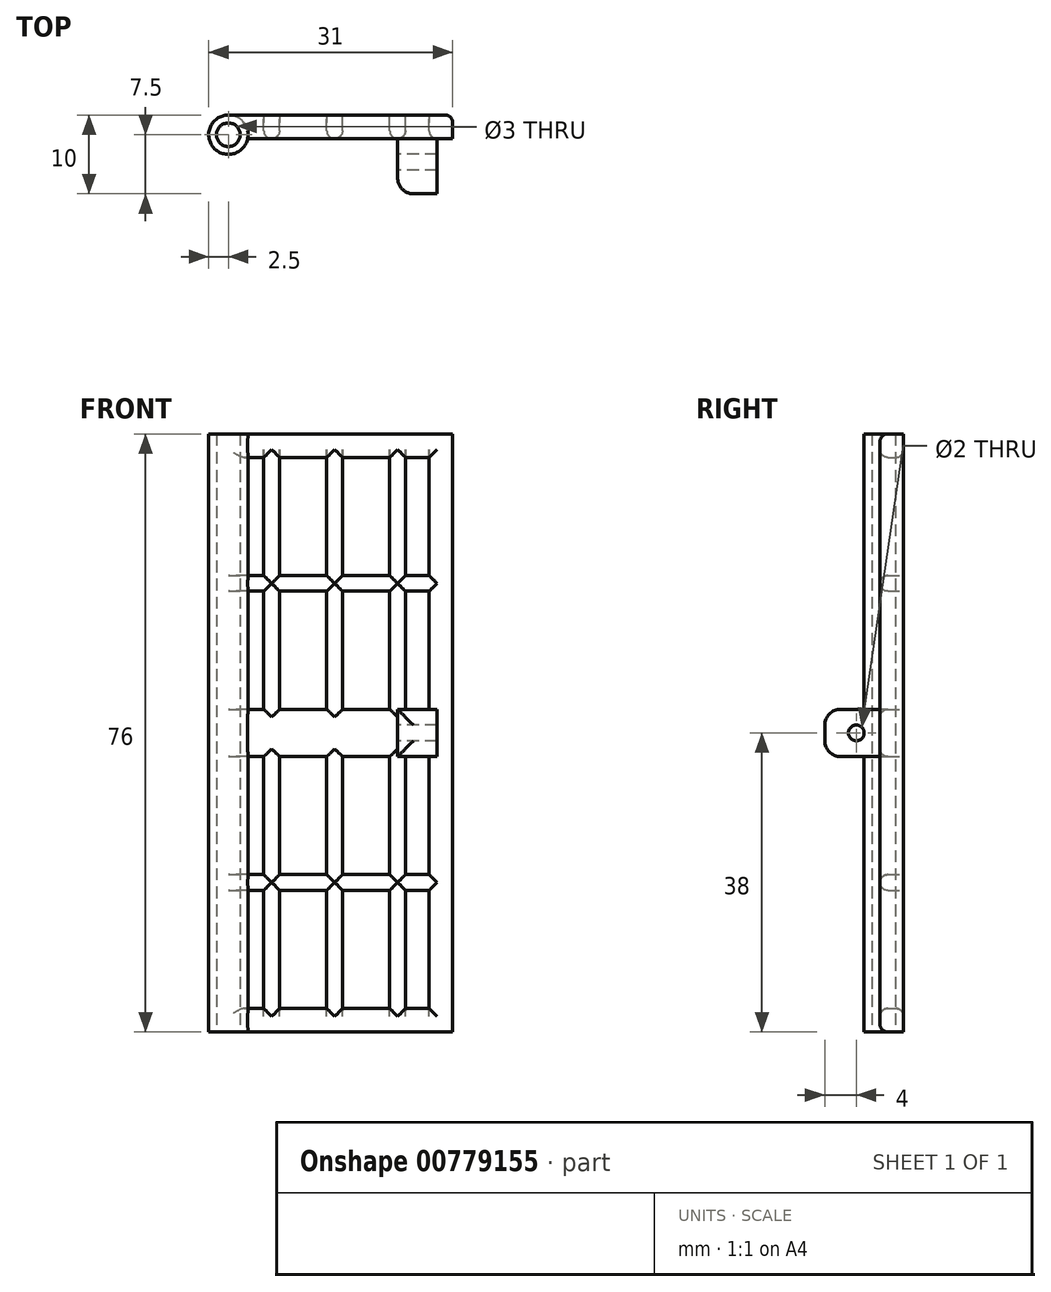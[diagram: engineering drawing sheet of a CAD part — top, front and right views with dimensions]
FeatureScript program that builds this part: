
annotation { "Feature Type Name" : "Feature", "Feature Type Description" : "" }
export const myFeature = defineFeature(function(context is Context, id is Id, definition is map)
    precondition{}
    {
        {
            var Q0;
            Q0=qCreatedBy(makeId("Front.planeOp"),FACE);
            var sketch = newSketch(context, id + "F0", { "sketchPlane" : qUnion([Q0])});
            skLineSegment(sketch, "E0.bottom", {"start": v(0, 0) * mm, "end": v(31, 0) * mm});
            skLineSegment(sketch, "E0.top", {"start": v(0, 76) * mm, "end": v(31, 76) * mm});
            skLineSegment(sketch, "E0.left", {"start": v(0, 0) * mm, "end": v(0, 76) * mm});
            skLineSegment(sketch, "E0.right", {"start": v(31, 0) * mm, "end": v(31, 76) * mm});
            skLineSegment(sketch, "E1.bottom", {"start": v(5, 73) * mm, "end": v(28, 73) * mm});
            skLineSegment(sketch, "E1.top", {"start": v(5, 3) * mm, "end": v(28, 3) * mm});
            skLineSegment(sketch, "E1.left", {"start": v(5, 73) * mm, "end": v(5, 3) * mm});
            skLineSegment(sketch, "E1.right", {"start": v(28, 73) * mm, "end": v(28, 3) * mm});
            skArc(sketch, "E2", {"start": v(23, 76) * mm, "mid": v(31, 84) * mm, "end": v(39, 76) * mm});
            skArc(sketch, "E3", {"start": v(25, 76) * mm, "mid": v(31, 82) * mm, "end": v(37, 76) * mm});
            skArc(sketch, "E4", {"start": v(17, 76) * mm, "mid": v(31, 90) * mm, "end": v(45, 76) * mm});
            skArc(sketch, "E5", {"start": v(15, 76) * mm, "mid": v(31, 92) * mm, "end": v(47, 76) * mm});
            skArc(sketch, "E6", {"start": v(9, 76) * mm, "mid": v(31, 98) * mm, "end": v(53, 76) * mm});
            skArc(sketch, "E7", {"start": v(7, 76) * mm, "mid": v(31, 100) * mm, "end": v(55, 76) * mm});
            skLineSegment(sketch, "E8", {"start": v(7, 76) * mm, "end": v(7, 3) * mm});
            skLineSegment(sketch, "E9", {"start": v(9, 76) * mm, "end": v(9, 3) * mm});
            skLineSegment(sketch, "E10", {"start": v(15, 76) * mm, "end": v(15, 3) * mm});
            skLineSegment(sketch, "E11", {"start": v(17, 76) * mm, "end": v(17, 3) * mm});
            skLineSegment(sketch, "E12", {"start": v(23, 76) * mm, "end": v(23, 3) * mm});
            skLineSegment(sketch, "E13", {"start": v(25, 76) * mm, "end": v(25, 3) * mm});
            skLineSegment(sketch, "E14", {"start": v(5, 58) * mm, "end": v(28, 58) * mm});
            skLineSegment(sketch, "E15", {"start": v(5, 56) * mm, "end": v(28, 56) * mm});
            skLineSegment(sketch, "E16", {"start": v(5, 41) * mm, "end": v(28, 41) * mm});
            skLineSegment(sketch, "E17", {"start": v(5, 35) * mm, "end": v(28, 35) * mm});
            skLineSegment(sketch, "E18", {"start": v(5, 18) * mm, "end": v(28, 18) * mm});
            skLineSegment(sketch, "E19", {"start": v(5, 20) * mm, "end": v(28, 20) * mm});
            skSolve(sketch);
        }
        {
            var Q0;
            {var subQ0=sQuery(id+"F0.wireOp",EDGE,"E10");var subQ1=sQuery(id+"F0.wireOp",EDGE,"E0.top");var subQ2=makeQuery(id+"F0.imprint","INTERSECT",VERTEX,{"derivedFrom":[subQ1,subQ0]});Q0=makeQuery(id+"F0.imprint","IMPRINT",FACE,{"disambiguationData":[TD([[makeQuery(id+"F0.imprint","IMPRINT",EDGE,{"disambiguationData":[TD([[subQ2,1.0]])],"derivedFrom":subQ1}),-1.0]])]});}
            var Q1;
            {var subQ0=sQuery(id+"F0.wireOp",EDGE,"E14");var subQ1=sQuery(id+"F0.wireOp",EDGE,"E9");var subQ2=makeQuery(id+"F0.imprint","INTERSECT",VERTEX,{"derivedFrom":[subQ1,subQ0]});Q1=makeQuery(id+"F0.imprint","IMPRINT",FACE,{"disambiguationData":[TD([[makeQuery(id+"F0.imprint","IMPRINT",EDGE,{"disambiguationData":[TD([[subQ2,-1.0]])],"derivedFrom":subQ1}),1.0]])]});}
            var Q2;
            {var subQ0=sQuery(id+"F0.wireOp",EDGE,"E16");var subQ1=sQuery(id+"F0.wireOp",EDGE,"E9");var subQ2=makeQuery(id+"F0.imprint","INTERSECT",VERTEX,{"derivedFrom":[subQ1,subQ0]});Q2=makeQuery(id+"F0.imprint","IMPRINT",FACE,{"disambiguationData":[TD([[makeQuery(id+"F0.imprint","IMPRINT",EDGE,{"disambiguationData":[TD([[subQ2,-1.0]])],"derivedFrom":subQ1}),1.0]])]});}
            var Q3;
            {var subQ0=sQuery(id+"F0.wireOp",EDGE,"E19");var subQ1=sQuery(id+"F0.wireOp",EDGE,"E9");var subQ2=makeQuery(id+"F0.imprint","INTERSECT",VERTEX,{"derivedFrom":[subQ1,subQ0]});Q3=makeQuery(id+"F0.imprint","IMPRINT",FACE,{"disambiguationData":[TD([[makeQuery(id+"F0.imprint","IMPRINT",EDGE,{"disambiguationData":[TD([[subQ2,-1.0]])],"derivedFrom":subQ1}),1.0]])]});}
            var Q4;
            Q4=makeQuery(id+"F0.imprint","IMPRINT",FACE,{"disambiguationData":[TD([[makeQuery(id+"F0.imprint","IMPRINT",EDGE,{"derivedFrom":sQuery(id+"F0.wireOp",EDGE,"E0.bottom")}),1.0]])]});
            var Q5;
            {var subQ0=sQuery(id+"F0.wireOp",EDGE,"E9");var subQ1=sQuery(id+"F0.wireOp",EDGE,"E0.top");var subQ2=makeQuery(id+"F0.imprint","INTERSECT",VERTEX,{"derivedFrom":[subQ1,subQ0]});Q5=makeQuery(id+"F0.imprint","IMPRINT",FACE,{"disambiguationData":[TD([[makeQuery(id+"F0.imprint","IMPRINT",EDGE,{"disambiguationData":[TD([[subQ2,1.0]])],"derivedFrom":subQ1}),-1.0]])]});}
            var Q6;
            {var subQ0=sQuery(id+"F0.wireOp",EDGE,"E11");var subQ1=sQuery(id+"F0.wireOp",EDGE,"E0.top");var subQ2=makeQuery(id+"F0.imprint","INTERSECT",VERTEX,{"derivedFrom":[subQ1,subQ0]});Q6=makeQuery(id+"F0.imprint","IMPRINT",FACE,{"disambiguationData":[TD([[makeQuery(id+"F0.imprint","IMPRINT",EDGE,{"disambiguationData":[TD([[subQ2,1.0]])],"derivedFrom":subQ1}),-1.0]])]});}
            var Q7;
            {var subQ0=sQuery(id+"F0.wireOp",EDGE,"E12");var subQ1=sQuery(id+"F0.wireOp",EDGE,"E0.top");var subQ2=makeQuery(id+"F0.imprint","INTERSECT",VERTEX,{"derivedFrom":[subQ1,subQ0]});Q7=makeQuery(id+"F0.imprint","IMPRINT",FACE,{"disambiguationData":[TD([[makeQuery(id+"F0.imprint","IMPRINT",EDGE,{"disambiguationData":[TD([[subQ2,1.0]])],"derivedFrom":subQ1}),-1.0]])]});}
            var Q8;
            {var subQ0=sQuery(id+"F0.wireOp",EDGE,"E12");var subQ1=sQuery(id+"F0.wireOp",EDGE,"E0.top");var subQ2=makeQuery(id+"F0.imprint","INTERSECT",VERTEX,{"derivedFrom":[subQ1,subQ0]});Q8=makeQuery(id+"F0.imprint","IMPRINT",FACE,{"disambiguationData":[TD([[makeQuery(id+"F0.imprint","IMPRINT",EDGE,{"disambiguationData":[TD([[subQ2,-1.0]])],"derivedFrom":subQ1}),-1.0]])]});}
            var Q9;
            {var subQ0=sQuery(id+"F0.wireOp",EDGE,"E8");var subQ1=sQuery(id+"F0.wireOp",EDGE,"E1.bottom");var subQ2=makeQuery(id+"F0.imprint","INTERSECT",VERTEX,{"derivedFrom":[subQ1,subQ0]});Q9=makeQuery(id+"F0.imprint","IMPRINT",FACE,{"disambiguationData":[TD([[makeQuery(id+"F0.imprint","IMPRINT",EDGE,{"disambiguationData":[TD([[subQ2,-1.0]])],"derivedFrom":subQ1}),-1.0]])]});}
            var Q10;
            {var subQ0=sQuery(id+"F0.wireOp",EDGE,"E10");var subQ1=sQuery(id+"F0.wireOp",EDGE,"E1.bottom");var subQ2=makeQuery(id+"F0.imprint","INTERSECT",VERTEX,{"derivedFrom":[subQ1,subQ0]});Q10=makeQuery(id+"F0.imprint","IMPRINT",FACE,{"disambiguationData":[TD([[makeQuery(id+"F0.imprint","IMPRINT",EDGE,{"disambiguationData":[TD([[subQ2,-1.0]])],"derivedFrom":subQ1}),-1.0]])]});}
            var Q11;
            {var subQ0=sQuery(id+"F0.wireOp",EDGE,"E12");var subQ1=sQuery(id+"F0.wireOp",EDGE,"E1.bottom");var subQ2=makeQuery(id+"F0.imprint","INTERSECT",VERTEX,{"derivedFrom":[subQ1,subQ0]});Q11=makeQuery(id+"F0.imprint","IMPRINT",FACE,{"disambiguationData":[TD([[makeQuery(id+"F0.imprint","IMPRINT",EDGE,{"disambiguationData":[TD([[subQ2,-1.0]])],"derivedFrom":subQ1}),-1.0]])]});}
            var Q12;
            {var subQ0=sQuery(id+"F0.wireOp",EDGE,"E14");var subQ1=sQuery(id+"F0.wireOp",EDGE,"E1.left");var subQ2=makeQuery(id+"F0.imprint","INTERSECT",VERTEX,{"derivedFrom":[subQ1,subQ0]});Q12=makeQuery(id+"F0.imprint","IMPRINT",FACE,{"disambiguationData":[TD([[makeQuery(id+"F0.imprint","IMPRINT",EDGE,{"disambiguationData":[TD([[subQ2,-1.0]])],"derivedFrom":subQ1}),1.0]])]});}
            var Q13;
            {var subQ0=sQuery(id+"F0.wireOp",EDGE,"E14");var subQ1=sQuery(id+"F0.wireOp",EDGE,"E8");var subQ2=makeQuery(id+"F0.imprint","INTERSECT",VERTEX,{"derivedFrom":[subQ1,subQ0]});Q13=makeQuery(id+"F0.imprint","IMPRINT",FACE,{"disambiguationData":[TD([[makeQuery(id+"F0.imprint","IMPRINT",EDGE,{"disambiguationData":[TD([[subQ2,-1.0]])],"derivedFrom":subQ1}),1.0]])]});}
            var Q14;
            {var subQ0=sQuery(id+"F0.wireOp",EDGE,"E14");var subQ1=sQuery(id+"F0.wireOp",EDGE,"E10");var subQ2=makeQuery(id+"F0.imprint","INTERSECT",VERTEX,{"derivedFrom":[subQ1,subQ0]});Q14=makeQuery(id+"F0.imprint","IMPRINT",FACE,{"disambiguationData":[TD([[makeQuery(id+"F0.imprint","IMPRINT",EDGE,{"disambiguationData":[TD([[subQ2,-1.0]])],"derivedFrom":subQ1}),1.0]])]});}
            var Q15;
            {var subQ0=sQuery(id+"F0.wireOp",EDGE,"E14");var subQ1=sQuery(id+"F0.wireOp",EDGE,"E11");var subQ2=makeQuery(id+"F0.imprint","INTERSECT",VERTEX,{"derivedFrom":[subQ1,subQ0]});Q15=makeQuery(id+"F0.imprint","IMPRINT",FACE,{"disambiguationData":[TD([[makeQuery(id+"F0.imprint","IMPRINT",EDGE,{"disambiguationData":[TD([[subQ2,-1.0]])],"derivedFrom":subQ1}),1.0]])]});}
            var Q16;
            {var subQ0=sQuery(id+"F0.wireOp",EDGE,"E14");var subQ1=sQuery(id+"F0.wireOp",EDGE,"E12");var subQ2=makeQuery(id+"F0.imprint","INTERSECT",VERTEX,{"derivedFrom":[subQ1,subQ0]});Q16=makeQuery(id+"F0.imprint","IMPRINT",FACE,{"disambiguationData":[TD([[makeQuery(id+"F0.imprint","IMPRINT",EDGE,{"disambiguationData":[TD([[subQ2,-1.0]])],"derivedFrom":subQ1}),1.0]])]});}
            var Q17;
            {var subQ0=sQuery(id+"F0.wireOp",EDGE,"E14");var subQ1=sQuery(id+"F0.wireOp",EDGE,"E1.right");var subQ2=makeQuery(id+"F0.imprint","INTERSECT",VERTEX,{"derivedFrom":[subQ1,subQ0]});Q17=makeQuery(id+"F0.imprint","IMPRINT",FACE,{"disambiguationData":[TD([[makeQuery(id+"F0.imprint","IMPRINT",EDGE,{"disambiguationData":[TD([[subQ2,-1.0]])],"derivedFrom":subQ1}),-1.0]])]});}
            var Q18;
            {var subQ0=sQuery(id+"F0.wireOp",EDGE,"E15");var subQ1=sQuery(id+"F0.wireOp",EDGE,"E10");var subQ2=makeQuery(id+"F0.imprint","INTERSECT",VERTEX,{"derivedFrom":[subQ1,subQ0]});Q18=makeQuery(id+"F0.imprint","IMPRINT",FACE,{"disambiguationData":[TD([[makeQuery(id+"F0.imprint","IMPRINT",EDGE,{"disambiguationData":[TD([[subQ2,-1.0]])],"derivedFrom":subQ1}),1.0]])]});}
            var Q19;
            {var subQ0=sQuery(id+"F0.wireOp",EDGE,"E15");var subQ1=sQuery(id+"F0.wireOp",EDGE,"E12");var subQ2=makeQuery(id+"F0.imprint","INTERSECT",VERTEX,{"derivedFrom":[subQ1,subQ0]});Q19=makeQuery(id+"F0.imprint","IMPRINT",FACE,{"disambiguationData":[TD([[makeQuery(id+"F0.imprint","IMPRINT",EDGE,{"disambiguationData":[TD([[subQ2,-1.0]])],"derivedFrom":subQ1}),1.0]])]});}
            var Q20;
            {var subQ0=sQuery(id+"F0.wireOp",EDGE,"E15");var subQ1=sQuery(id+"F0.wireOp",EDGE,"E8");var subQ2=makeQuery(id+"F0.imprint","INTERSECT",VERTEX,{"derivedFrom":[subQ1,subQ0]});Q20=makeQuery(id+"F0.imprint","IMPRINT",FACE,{"disambiguationData":[TD([[makeQuery(id+"F0.imprint","IMPRINT",EDGE,{"disambiguationData":[TD([[subQ2,-1.0]])],"derivedFrom":subQ1}),1.0]])]});}
            var Q21;
            {var subQ0=sQuery(id+"F0.wireOp",EDGE,"E16");var subQ1=sQuery(id+"F0.wireOp",EDGE,"E1.left");var subQ2=makeQuery(id+"F0.imprint","INTERSECT",VERTEX,{"derivedFrom":[subQ1,subQ0]});Q21=makeQuery(id+"F0.imprint","IMPRINT",FACE,{"disambiguationData":[TD([[makeQuery(id+"F0.imprint","IMPRINT",EDGE,{"disambiguationData":[TD([[subQ2,-1.0]])],"derivedFrom":subQ1}),1.0]])]});}
            var Q22;
            {var subQ0=sQuery(id+"F0.wireOp",EDGE,"E16");var subQ1=sQuery(id+"F0.wireOp",EDGE,"E8");var subQ2=makeQuery(id+"F0.imprint","INTERSECT",VERTEX,{"derivedFrom":[subQ1,subQ0]});Q22=makeQuery(id+"F0.imprint","IMPRINT",FACE,{"disambiguationData":[TD([[makeQuery(id+"F0.imprint","IMPRINT",EDGE,{"disambiguationData":[TD([[subQ2,-1.0]])],"derivedFrom":subQ1}),1.0]])]});}
            var Q23;
            {var subQ0=sQuery(id+"F0.wireOp",EDGE,"E16");var subQ1=sQuery(id+"F0.wireOp",EDGE,"E10");var subQ2=makeQuery(id+"F0.imprint","INTERSECT",VERTEX,{"derivedFrom":[subQ1,subQ0]});Q23=makeQuery(id+"F0.imprint","IMPRINT",FACE,{"disambiguationData":[TD([[makeQuery(id+"F0.imprint","IMPRINT",EDGE,{"disambiguationData":[TD([[subQ2,-1.0]])],"derivedFrom":subQ1}),1.0]])]});}
            var Q24;
            {var subQ0=sQuery(id+"F0.wireOp",EDGE,"E16");var subQ1=sQuery(id+"F0.wireOp",EDGE,"E11");var subQ2=makeQuery(id+"F0.imprint","INTERSECT",VERTEX,{"derivedFrom":[subQ1,subQ0]});Q24=makeQuery(id+"F0.imprint","IMPRINT",FACE,{"disambiguationData":[TD([[makeQuery(id+"F0.imprint","IMPRINT",EDGE,{"disambiguationData":[TD([[subQ2,-1.0]])],"derivedFrom":subQ1}),1.0]])]});}
            var Q25;
            {var subQ0=sQuery(id+"F0.wireOp",EDGE,"E16");var subQ1=sQuery(id+"F0.wireOp",EDGE,"E12");var subQ2=makeQuery(id+"F0.imprint","INTERSECT",VERTEX,{"derivedFrom":[subQ1,subQ0]});Q25=makeQuery(id+"F0.imprint","IMPRINT",FACE,{"disambiguationData":[TD([[makeQuery(id+"F0.imprint","IMPRINT",EDGE,{"disambiguationData":[TD([[subQ2,-1.0]])],"derivedFrom":subQ1}),1.0]])]});}
            var Q26;
            {var subQ0=sQuery(id+"F0.wireOp",EDGE,"E16");var subQ1=sQuery(id+"F0.wireOp",EDGE,"E1.right");var subQ2=makeQuery(id+"F0.imprint","INTERSECT",VERTEX,{"derivedFrom":[subQ1,subQ0]});Q26=makeQuery(id+"F0.imprint","IMPRINT",FACE,{"disambiguationData":[TD([[makeQuery(id+"F0.imprint","IMPRINT",EDGE,{"disambiguationData":[TD([[subQ2,-1.0]])],"derivedFrom":subQ1}),-1.0]])]});}
            var Q27;
            {var subQ0=sQuery(id+"F0.wireOp",EDGE,"E8");var subQ1=sQuery(id+"F0.wireOp",EDGE,"E1.top");var subQ2=makeQuery(id+"F0.imprint","INTERSECT",VERTEX,{"derivedFrom":[subQ1,subQ0]});Q27=makeQuery(id+"F0.imprint","IMPRINT",FACE,{"disambiguationData":[TD([[makeQuery(id+"F0.imprint","IMPRINT",EDGE,{"disambiguationData":[TD([[subQ2,-1.0]])],"derivedFrom":subQ1}),1.0]])]});}
            var Q28;
            {var subQ0=sQuery(id+"F0.wireOp",EDGE,"E17");var subQ1=sQuery(id+"F0.wireOp",EDGE,"E8");var subQ2=makeQuery(id+"F0.imprint","INTERSECT",VERTEX,{"derivedFrom":[subQ1,subQ0]});Q28=makeQuery(id+"F0.imprint","IMPRINT",FACE,{"disambiguationData":[TD([[makeQuery(id+"F0.imprint","IMPRINT",EDGE,{"disambiguationData":[TD([[subQ2,-1.0]])],"derivedFrom":subQ1}),1.0]])]});}
            var Q29;
            {var subQ0=sQuery(id+"F0.wireOp",EDGE,"E19");var subQ1=sQuery(id+"F0.wireOp",EDGE,"E8");var subQ2=makeQuery(id+"F0.imprint","INTERSECT",VERTEX,{"derivedFrom":[subQ1,subQ0]});Q29=makeQuery(id+"F0.imprint","IMPRINT",FACE,{"disambiguationData":[TD([[makeQuery(id+"F0.imprint","IMPRINT",EDGE,{"disambiguationData":[TD([[subQ2,-1.0]])],"derivedFrom":subQ1}),1.0]])]});}
            var Q30;
            {var subQ0=sQuery(id+"F0.wireOp",EDGE,"E17");var subQ1=sQuery(id+"F0.wireOp",EDGE,"E10");var subQ2=makeQuery(id+"F0.imprint","INTERSECT",VERTEX,{"derivedFrom":[subQ1,subQ0]});Q30=makeQuery(id+"F0.imprint","IMPRINT",FACE,{"disambiguationData":[TD([[makeQuery(id+"F0.imprint","IMPRINT",EDGE,{"disambiguationData":[TD([[subQ2,-1.0]])],"derivedFrom":subQ1}),1.0]])]});}
            var Q31;
            {var subQ0=sQuery(id+"F0.wireOp",EDGE,"E17");var subQ1=sQuery(id+"F0.wireOp",EDGE,"E12");var subQ2=makeQuery(id+"F0.imprint","INTERSECT",VERTEX,{"derivedFrom":[subQ1,subQ0]});Q31=makeQuery(id+"F0.imprint","IMPRINT",FACE,{"disambiguationData":[TD([[makeQuery(id+"F0.imprint","IMPRINT",EDGE,{"disambiguationData":[TD([[subQ2,-1.0]])],"derivedFrom":subQ1}),1.0]])]});}
            var Q32;
            {var subQ0=sQuery(id+"F0.wireOp",EDGE,"E18");var subQ1=sQuery(id+"F0.wireOp",EDGE,"E1.right");var subQ2=makeQuery(id+"F0.imprint","INTERSECT",VERTEX,{"derivedFrom":[subQ1,subQ0]});Q32=makeQuery(id+"F0.imprint","IMPRINT",FACE,{"disambiguationData":[TD([[makeQuery(id+"F0.imprint","IMPRINT",EDGE,{"disambiguationData":[TD([[subQ2,1.0]])],"derivedFrom":subQ1}),-1.0]])]});}
            var Q33;
            {var subQ0=sQuery(id+"F0.wireOp",EDGE,"E12");var subQ1=sQuery(id+"F0.wireOp",EDGE,"E1.top");var subQ2=makeQuery(id+"F0.imprint","INTERSECT",VERTEX,{"derivedFrom":[subQ1,subQ0]});Q33=makeQuery(id+"F0.imprint","IMPRINT",FACE,{"disambiguationData":[TD([[makeQuery(id+"F0.imprint","IMPRINT",EDGE,{"disambiguationData":[TD([[subQ2,-1.0]])],"derivedFrom":subQ1}),1.0]])]});}
            var Q34;
            {var subQ0=sQuery(id+"F0.wireOp",EDGE,"E19");var subQ1=sQuery(id+"F0.wireOp",EDGE,"E12");var subQ2=makeQuery(id+"F0.imprint","INTERSECT",VERTEX,{"derivedFrom":[subQ1,subQ0]});Q34=makeQuery(id+"F0.imprint","IMPRINT",FACE,{"disambiguationData":[TD([[makeQuery(id+"F0.imprint","IMPRINT",EDGE,{"disambiguationData":[TD([[subQ2,-1.0]])],"derivedFrom":subQ1}),1.0]])]});}
            var Q35;
            {var subQ0=sQuery(id+"F0.wireOp",EDGE,"E19");var subQ1=sQuery(id+"F0.wireOp",EDGE,"E11");var subQ2=makeQuery(id+"F0.imprint","INTERSECT",VERTEX,{"derivedFrom":[subQ1,subQ0]});Q35=makeQuery(id+"F0.imprint","IMPRINT",FACE,{"disambiguationData":[TD([[makeQuery(id+"F0.imprint","IMPRINT",EDGE,{"disambiguationData":[TD([[subQ2,-1.0]])],"derivedFrom":subQ1}),1.0]])]});}
            var Q36;
            {var subQ0=sQuery(id+"F0.wireOp",EDGE,"E10");var subQ1=sQuery(id+"F0.wireOp",EDGE,"E1.top");var subQ2=makeQuery(id+"F0.imprint","INTERSECT",VERTEX,{"derivedFrom":[subQ1,subQ0]});Q36=makeQuery(id+"F0.imprint","IMPRINT",FACE,{"disambiguationData":[TD([[makeQuery(id+"F0.imprint","IMPRINT",EDGE,{"disambiguationData":[TD([[subQ2,-1.0]])],"derivedFrom":subQ1}),1.0]])]});}
            var Q37;
            {var subQ0=sQuery(id+"F0.wireOp",EDGE,"E19");var subQ1=sQuery(id+"F0.wireOp",EDGE,"E10");var subQ2=makeQuery(id+"F0.imprint","INTERSECT",VERTEX,{"derivedFrom":[subQ1,subQ0]});Q37=makeQuery(id+"F0.imprint","IMPRINT",FACE,{"disambiguationData":[TD([[makeQuery(id+"F0.imprint","IMPRINT",EDGE,{"disambiguationData":[TD([[subQ2,-1.0]])],"derivedFrom":subQ1}),1.0]])]});}
            var Q38;
            {var subQ0=sQuery(id+"F0.wireOp",EDGE,"E18");var subQ1=sQuery(id+"F0.wireOp",EDGE,"E1.left");var subQ2=makeQuery(id+"F0.imprint","INTERSECT",VERTEX,{"derivedFrom":[subQ1,subQ0]});Q38=makeQuery(id+"F0.imprint","IMPRINT",FACE,{"disambiguationData":[TD([[makeQuery(id+"F0.imprint","IMPRINT",EDGE,{"disambiguationData":[TD([[subQ2,1.0]])],"derivedFrom":subQ1}),1.0]])]});}
            extrude(context, id + "F1", {"entities" : qUnion([Q0, Q1, Q2, Q3, Q4, Q5, Q6, Q7, Q8, Q9, Q10, Q11, Q12, Q13, Q14, Q15, Q16, Q17, Q18, Q19, Q20, Q21, Q22, Q23, Q24, Q25, Q26, Q27, Q28, Q29, Q30, Q31, Q32, Q33, Q34, Q35, Q36, Q37, Q38]), "depth" : 3 * mm, "offsetDistance" : 25 * mm});
        }
        {
            var Q0;
            Q0=qCreatedBy(makeId("Top.planeOp"),FACE);
            var sketch = newSketch(context, id + "F2", { "sketchPlane" : qUnion([Q0])});
            skPoint(sketch, "E20", {"position": v(2.5, -2.5) * mm});
            skLineSegment(sketch, "E21.bottom", {"start": v(0, 0) * mm, "end": v(5, 0) * mm});
            skLineSegment(sketch, "E21.top", {"start": v(0, -5) * mm, "end": v(5, -5) * mm});
            skLineSegment(sketch, "E21.left", {"start": v(0, 0) * mm, "end": v(0, -5) * mm});
            skLineSegment(sketch, "E21.right", {"start": v(5, 0) * mm, "end": v(5, -5) * mm});
            skSolve(sketch);
        }
        {
            var Q0;
            Q0=makeQuery(id+"F2.imprint","IMPRINT",FACE,{"disambiguationData":[TD([[makeQuery(id+"F2.imprint","IMPRINT",EDGE,{"derivedFrom":sQuery(id+"F2.wireOp",EDGE,"E21.bottom")}),-1.0]])]});
            var Q1;
            Q1=makeQuery(id+"F2.imprint","IMPRINT",FACE,{"disambiguationData":[TD([[makeQuery(id+"F2.imprint","IMPRINT",EDGE,{"derivedFrom":sQuery(id+"F2.wireOp",EDGE,"dONhVUND-5mgP-4hEB-Uarb-gnFvTBPlQlVB.bottom")}),1.0]])]});
            var Q2;
            Q2=makeQuery(id+"F2.imprint","IMPRINT",FACE,{"disambiguationData":[TD([[makeQuery(id+"F2.imprint","IMPRINT",EDGE,{"derivedFrom":sQuery(id+"F2.wireOp",EDGE,"KLBum8TW-YJ0B-5sS5-SbCJ-48z4D2TFME6R.top")}),1.0]])]});
            extrude(context, id + "F3", {"entities" : qUnion([Q0, Q1, Q2]), "operationType" : NewBodyOperationType.ADD, "depth" : 76 * mm, "offsetDistance" : 25 * mm});
        }
        {
            var Q0;
            Q0=qCreatedBy(makeId("Top.planeOp"),FACE);
            var sketch = newSketch(context, id + "F4", { "sketchPlane" : qUnion([Q0])});
            skPoint(sketch, "E22", {"position": v(2.5, -2.5) * mm});
            skSolve(sketch);
        }
        {
            var Q0;
            Q0=sQuery(id+"F4.wireOp",VERTEX,"E22");
            var Q1;
            Q1=makeQuery(id+"F1.opExtrude","SWEPT_BODY",BODY,{"disambiguationData":[OSD([sQuery(id+"F0.wireOp",EDGE,"E0.bottom"),sQuery(id+"F0.wireOp",EDGE,"E0.top"),sQuery(id+"F0.wireOp",EDGE,"E0.left"),sQuery(id+"F0.wireOp",EDGE,"E0.right"),sQuery(id+"F0.wireOp",EDGE,"E1.bottom"),sQuery(id+"F0.wireOp",EDGE,"E1.top"),sQuery(id+"F0.wireOp",EDGE,"E1.left"),sQuery(id+"F0.wireOp",EDGE,"E1.right"),sQuery(id+"F0.wireOp",EDGE,"E8"),sQuery(id+"F0.wireOp",EDGE,"E9"),sQuery(id+"F0.wireOp",EDGE,"E10"),sQuery(id+"F0.wireOp",EDGE,"E11"),sQuery(id+"F0.wireOp",EDGE,"E12"),sQuery(id+"F0.wireOp",EDGE,"E13"),sQuery(id+"F0.wireOp",EDGE,"E14"),sQuery(id+"F0.wireOp",EDGE,"E15"),sQuery(id+"F0.wireOp",EDGE,"E16"),sQuery(id+"F0.wireOp",EDGE,"E17"),sQuery(id+"F0.wireOp",EDGE,"E18"),sQuery(id+"F0.wireOp",EDGE,"E19")])]});
            hole(context, id + "F5", {"style" : HoleStyle.SIMPLE, "endStyle" : HoleEndStyle.BLIND, "oppositeDirection" : true, "holeDiameter" : 3 * mm, "majorDiameter" : 5 * mm, "holeDepth" : 85 * mm, "isTappedThrough" : true, "tappedDepth" : 12 * mm, "tapClearance" : 3, "locations" : qUnion([Q0]), "scope" : qUnion([Q1])});
        }
        {
            var Q0;
            Q0=makeQuery(id+"F3.opExtrude","SWEPT_EDGE",EDGE,{"disambiguationData":[OSD([sQuery(id+"F2.wireOp",EDGE,"E21.top"),sQuery(id+"F2.wireOp",EDGE,"E21.right")])]});
            var Q1;
            Q1=makeQuery(id+"F3.opExtrude","SWEPT_EDGE",EDGE,{"disambiguationData":[OSD([sQuery(id+"F2.wireOp",EDGE,"E21.top"),sQuery(id+"F2.wireOp",EDGE,"E21.left")])]});
            var Q2;
            {var subQ0=sQuery(id+"F0.wireOp",EDGE,"E1.left");Q2=makeQuery(id+"F1.opExtrude","CAP_EDGE",EDGE,{"disambiguationData":[OSD([subQ0]),TDD([makeQuery(id+"F0.imprint","IMPRINT",EDGE,{"disambiguationData":[TD([[makeQuery(id+"F0.imprint","INTERSECT",VERTEX,{"derivedFrom":[sQuery(id+"F0.wireOp",EDGE,"E1.top"),subQ0]}),1.0]])],"derivedFrom":subQ0})])],"isStart":true});}
            var Q3;
            {var subQ0=sQuery(id+"F0.wireOp",EDGE,"E1.left");Q3=makeQuery(id+"F1.opExtrude","CAP_EDGE",EDGE,{"disambiguationData":[OSD([subQ0]),TDD([makeQuery(id+"F0.imprint","IMPRINT",EDGE,{"disambiguationData":[TD([[makeQuery(id+"F0.imprint","INTERSECT",VERTEX,{"derivedFrom":[subQ0,sQuery(id+"F0.wireOp",EDGE,"E17")]}),-1.0]])],"derivedFrom":subQ0})])],"isStart":true});}
            var Q4;
            {var subQ0=sQuery(id+"F0.wireOp",EDGE,"E1.left");Q4=makeQuery(id+"F1.opExtrude","CAP_EDGE",EDGE,{"disambiguationData":[OSD([subQ0]),TDD([makeQuery(id+"F0.imprint","IMPRINT",EDGE,{"disambiguationData":[TD([[makeQuery(id+"F0.imprint","INTERSECT",VERTEX,{"derivedFrom":[subQ0,sQuery(id+"F0.wireOp",EDGE,"E15")]}),-1.0]])],"derivedFrom":subQ0})])],"isStart":true});}
            var Q5;
            {var subQ0=sQuery(id+"F0.wireOp",EDGE,"E1.left");Q5=makeQuery(id+"F1.opExtrude","CAP_EDGE",EDGE,{"disambiguationData":[OSD([subQ0]),TDD([makeQuery(id+"F0.imprint","IMPRINT",EDGE,{"disambiguationData":[TD([[makeQuery(id+"F0.imprint","INTERSECT",VERTEX,{"derivedFrom":[sQuery(id+"F0.wireOp",EDGE,"E1.bottom"),subQ0]}),-1.0]])],"derivedFrom":subQ0})])],"isStart":true});}
            var Q6;
            Q6=makeQuery(id+"F1.opExtrude","CAP_EDGE",EDGE,{"disambiguationData":[OSD([sQuery(id+"F0.wireOp",EDGE,"E0.left")])],"isStart":true});
            fillet(context, id + "F6", {"entities" : qUnion([Q0, Q1, Q2, Q3, Q4, Q5, Q6]), "radius" : 2.5 * mm, "tangentPropagation" : true, "allowEdgeOverflow" : false});
        }
        {
            var Q0;
            Q0=makeQuery(id+"F1.opExtrude","CAP_EDGE",EDGE,{"disambiguationData":[OSD([sQuery(id+"F0.wireOp",EDGE,"E0.top")])],"isStart":false});
            var Q1;
            {var subQ0=sQuery(id+"F0.wireOp",EDGE,"E1.bottom");Q1=makeQuery(id+"F1.opExtrude","CAP_EDGE",EDGE,{"disambiguationData":[OSD([subQ0]),TDD([makeQuery(id+"F0.imprint","IMPRINT",EDGE,{"disambiguationData":[TD([[makeQuery(id+"F0.imprint","INTERSECT",VERTEX,{"derivedFrom":[subQ0,sQuery(id+"F0.wireOp",EDGE,"E9")]}),-1.0]])],"derivedFrom":subQ0})])],"isStart":false});}
            var Q2;
            {var subQ0=sQuery(id+"F0.wireOp",EDGE,"E1.bottom");Q2=makeQuery(id+"F1.opExtrude","CAP_EDGE",EDGE,{"disambiguationData":[OSD([subQ0]),TDD([makeQuery(id+"F0.imprint","IMPRINT",EDGE,{"disambiguationData":[TD([[makeQuery(id+"F0.imprint","INTERSECT",VERTEX,{"derivedFrom":[subQ0,sQuery(id+"F0.wireOp",EDGE,"E1.left")]}),-1.0]])],"derivedFrom":subQ0})])],"isStart":false});}
            var Q3;
            {var subQ0=sQuery(id+"F0.wireOp",EDGE,"E8");Q3=makeQuery(id+"F1.opExtrude","CAP_EDGE",EDGE,{"disambiguationData":[OSD([subQ0]),TDD([makeQuery(id+"F0.imprint","IMPRINT",EDGE,{"disambiguationData":[TD([[makeQuery(id+"F0.imprint","INTERSECT",VERTEX,{"derivedFrom":[sQuery(id+"F0.wireOp",EDGE,"E1.bottom"),subQ0]}),-1.0]])],"derivedFrom":subQ0})])],"isStart":false});}
            var Q4;
            {var subQ0=sQuery(id+"F0.wireOp",EDGE,"E10");Q4=makeQuery(id+"F1.opExtrude","CAP_EDGE",EDGE,{"disambiguationData":[OSD([subQ0]),TDD([makeQuery(id+"F0.imprint","IMPRINT",EDGE,{"disambiguationData":[TD([[makeQuery(id+"F0.imprint","INTERSECT",VERTEX,{"derivedFrom":[sQuery(id+"F0.wireOp",EDGE,"E1.bottom"),subQ0]}),-1.0]])],"derivedFrom":subQ0})])],"isStart":false});}
            var Q5;
            {var subQ0=sQuery(id+"F0.wireOp",EDGE,"E1.bottom");Q5=makeQuery(id+"F1.opExtrude","CAP_EDGE",EDGE,{"disambiguationData":[OSD([subQ0]),TDD([makeQuery(id+"F0.imprint","IMPRINT",EDGE,{"disambiguationData":[TD([[makeQuery(id+"F0.imprint","INTERSECT",VERTEX,{"derivedFrom":[subQ0,sQuery(id+"F0.wireOp",EDGE,"E11")]}),-1.0]])],"derivedFrom":subQ0})])],"isStart":false});}
            var Q6;
            {var subQ0=sQuery(id+"F0.wireOp",EDGE,"E1.bottom");Q6=makeQuery(id+"F1.opExtrude","CAP_EDGE",EDGE,{"disambiguationData":[OSD([subQ0]),TDD([makeQuery(id+"F0.imprint","IMPRINT",EDGE,{"disambiguationData":[TD([[makeQuery(id+"F0.imprint","INTERSECT",VERTEX,{"derivedFrom":[subQ0,sQuery(id+"F0.wireOp",EDGE,"E1.right")]}),1.0]])],"derivedFrom":subQ0})])],"isStart":false});}
            var Q7;
            {var subQ0=sQuery(id+"F0.wireOp",EDGE,"E13");Q7=makeQuery(id+"F1.opExtrude","CAP_EDGE",EDGE,{"disambiguationData":[OSD([subQ0]),TDD([makeQuery(id+"F0.imprint","IMPRINT",EDGE,{"disambiguationData":[TD([[makeQuery(id+"F0.imprint","INTERSECT",VERTEX,{"derivedFrom":[sQuery(id+"F0.wireOp",EDGE,"E1.bottom"),subQ0]}),-1.0]])],"derivedFrom":subQ0})])],"isStart":false});}
            var Q8;
            {var subQ0=sQuery(id+"F0.wireOp",EDGE,"E12");Q8=makeQuery(id+"F1.opExtrude","CAP_EDGE",EDGE,{"disambiguationData":[OSD([subQ0]),TDD([makeQuery(id+"F0.imprint","IMPRINT",EDGE,{"disambiguationData":[TD([[makeQuery(id+"F0.imprint","INTERSECT",VERTEX,{"derivedFrom":[sQuery(id+"F0.wireOp",EDGE,"E1.bottom"),subQ0]}),-1.0]])],"derivedFrom":subQ0})])],"isStart":false});}
            var Q9;
            {var subQ0=sQuery(id+"F0.wireOp",EDGE,"E11");Q9=makeQuery(id+"F1.opExtrude","CAP_EDGE",EDGE,{"disambiguationData":[OSD([subQ0]),TDD([makeQuery(id+"F0.imprint","IMPRINT",EDGE,{"disambiguationData":[TD([[makeQuery(id+"F0.imprint","INTERSECT",VERTEX,{"derivedFrom":[sQuery(id+"F0.wireOp",EDGE,"E1.bottom"),subQ0]}),-1.0]])],"derivedFrom":subQ0})])],"isStart":false});}
            var Q10;
            {var subQ0=sQuery(id+"F0.wireOp",EDGE,"E9");Q10=makeQuery(id+"F1.opExtrude","CAP_EDGE",EDGE,{"disambiguationData":[OSD([subQ0]),TDD([makeQuery(id+"F0.imprint","IMPRINT",EDGE,{"disambiguationData":[TD([[makeQuery(id+"F0.imprint","INTERSECT",VERTEX,{"derivedFrom":[sQuery(id+"F0.wireOp",EDGE,"E1.bottom"),subQ0]}),-1.0]])],"derivedFrom":subQ0})])],"isStart":false});}
            var Q11;
            {var subQ0=sQuery(id+"F0.wireOp",EDGE,"E14");Q11=makeQuery(id+"F1.opExtrude","CAP_EDGE",EDGE,{"disambiguationData":[OSD([subQ0]),TDD([makeQuery(id+"F0.imprint","IMPRINT",EDGE,{"disambiguationData":[TD([[makeQuery(id+"F0.imprint","INTERSECT",VERTEX,{"derivedFrom":[sQuery(id+"F0.wireOp",EDGE,"E1.left"),subQ0]}),-1.0]])],"derivedFrom":subQ0})])],"isStart":false});}
            var Q12;
            {var subQ0=sQuery(id+"F0.wireOp",EDGE,"E14");Q12=makeQuery(id+"F1.opExtrude","CAP_EDGE",EDGE,{"disambiguationData":[OSD([subQ0]),TDD([makeQuery(id+"F0.imprint","IMPRINT",EDGE,{"disambiguationData":[TD([[makeQuery(id+"F0.imprint","INTERSECT",VERTEX,{"derivedFrom":[sQuery(id+"F0.wireOp",EDGE,"E9"),subQ0]}),-1.0]])],"derivedFrom":subQ0})])],"isStart":false});}
            var Q13;
            {var subQ0=sQuery(id+"F0.wireOp",EDGE,"E14");Q13=makeQuery(id+"F1.opExtrude","CAP_EDGE",EDGE,{"disambiguationData":[OSD([subQ0]),TDD([makeQuery(id+"F0.imprint","IMPRINT",EDGE,{"disambiguationData":[TD([[makeQuery(id+"F0.imprint","INTERSECT",VERTEX,{"derivedFrom":[sQuery(id+"F0.wireOp",EDGE,"E11"),subQ0]}),-1.0]])],"derivedFrom":subQ0})])],"isStart":false});}
            var Q14;
            {var subQ0=sQuery(id+"F0.wireOp",EDGE,"E14");Q14=makeQuery(id+"F1.opExtrude","CAP_EDGE",EDGE,{"disambiguationData":[OSD([subQ0]),TDD([makeQuery(id+"F0.imprint","IMPRINT",EDGE,{"disambiguationData":[TD([[makeQuery(id+"F0.imprint","INTERSECT",VERTEX,{"derivedFrom":[sQuery(id+"F0.wireOp",EDGE,"E1.right"),subQ0]}),1.0]])],"derivedFrom":subQ0})])],"isStart":false});}
            var Q15;
            {var subQ0=sQuery(id+"F0.wireOp",EDGE,"E15");Q15=makeQuery(id+"F1.opExtrude","CAP_EDGE",EDGE,{"disambiguationData":[OSD([subQ0]),TDD([makeQuery(id+"F0.imprint","IMPRINT",EDGE,{"disambiguationData":[TD([[makeQuery(id+"F0.imprint","INTERSECT",VERTEX,{"derivedFrom":[sQuery(id+"F0.wireOp",EDGE,"E1.right"),subQ0]}),1.0]])],"derivedFrom":subQ0})])],"isStart":false});}
            var Q16;
            {var subQ0=sQuery(id+"F0.wireOp",EDGE,"E15");Q16=makeQuery(id+"F1.opExtrude","CAP_EDGE",EDGE,{"disambiguationData":[OSD([subQ0]),TDD([makeQuery(id+"F0.imprint","IMPRINT",EDGE,{"disambiguationData":[TD([[makeQuery(id+"F0.imprint","INTERSECT",VERTEX,{"derivedFrom":[sQuery(id+"F0.wireOp",EDGE,"E11"),subQ0]}),-1.0]])],"derivedFrom":subQ0})])],"isStart":false});}
            var Q17;
            {var subQ0=sQuery(id+"F0.wireOp",EDGE,"E15");Q17=makeQuery(id+"F1.opExtrude","CAP_EDGE",EDGE,{"disambiguationData":[OSD([subQ0]),TDD([makeQuery(id+"F0.imprint","IMPRINT",EDGE,{"disambiguationData":[TD([[makeQuery(id+"F0.imprint","INTERSECT",VERTEX,{"derivedFrom":[sQuery(id+"F0.wireOp",EDGE,"E9"),subQ0]}),-1.0]])],"derivedFrom":subQ0})])],"isStart":false});}
            var Q18;
            {var subQ0=sQuery(id+"F0.wireOp",EDGE,"E15");Q18=makeQuery(id+"F1.opExtrude","CAP_EDGE",EDGE,{"disambiguationData":[OSD([subQ0]),TDD([makeQuery(id+"F0.imprint","IMPRINT",EDGE,{"disambiguationData":[TD([[makeQuery(id+"F0.imprint","INTERSECT",VERTEX,{"derivedFrom":[sQuery(id+"F0.wireOp",EDGE,"E1.left"),subQ0]}),-1.0]])],"derivedFrom":subQ0})])],"isStart":false});}
            var Q19;
            {var subQ0=sQuery(id+"F0.wireOp",EDGE,"E8");Q19=makeQuery(id+"F1.opExtrude","CAP_EDGE",EDGE,{"disambiguationData":[OSD([subQ0]),TDD([makeQuery(id+"F0.imprint","IMPRINT",EDGE,{"disambiguationData":[TD([[makeQuery(id+"F0.imprint","INTERSECT",VERTEX,{"derivedFrom":[subQ0,sQuery(id+"F0.wireOp",EDGE,"E15")]}),-1.0]])],"derivedFrom":subQ0})])],"isStart":false});}
            var Q20;
            {var subQ0=sQuery(id+"F0.wireOp",EDGE,"E9");Q20=makeQuery(id+"F1.opExtrude","CAP_EDGE",EDGE,{"disambiguationData":[OSD([subQ0]),TDD([makeQuery(id+"F0.imprint","IMPRINT",EDGE,{"disambiguationData":[TD([[makeQuery(id+"F0.imprint","INTERSECT",VERTEX,{"derivedFrom":[subQ0,sQuery(id+"F0.wireOp",EDGE,"E15")]}),-1.0]])],"derivedFrom":subQ0})])],"isStart":false});}
            var Q21;
            {var subQ0=sQuery(id+"F0.wireOp",EDGE,"E10");Q21=makeQuery(id+"F1.opExtrude","CAP_EDGE",EDGE,{"disambiguationData":[OSD([subQ0]),TDD([makeQuery(id+"F0.imprint","IMPRINT",EDGE,{"disambiguationData":[TD([[makeQuery(id+"F0.imprint","INTERSECT",VERTEX,{"derivedFrom":[subQ0,sQuery(id+"F0.wireOp",EDGE,"E15")]}),-1.0]])],"derivedFrom":subQ0})])],"isStart":false});}
            var Q22;
            {var subQ0=sQuery(id+"F0.wireOp",EDGE,"E11");Q22=makeQuery(id+"F1.opExtrude","CAP_EDGE",EDGE,{"disambiguationData":[OSD([subQ0]),TDD([makeQuery(id+"F0.imprint","IMPRINT",EDGE,{"disambiguationData":[TD([[makeQuery(id+"F0.imprint","INTERSECT",VERTEX,{"derivedFrom":[subQ0,sQuery(id+"F0.wireOp",EDGE,"E15")]}),-1.0]])],"derivedFrom":subQ0})])],"isStart":false});}
            var Q23;
            {var subQ0=sQuery(id+"F0.wireOp",EDGE,"E12");Q23=makeQuery(id+"F1.opExtrude","CAP_EDGE",EDGE,{"disambiguationData":[OSD([subQ0]),TDD([makeQuery(id+"F0.imprint","IMPRINT",EDGE,{"disambiguationData":[TD([[makeQuery(id+"F0.imprint","INTERSECT",VERTEX,{"derivedFrom":[subQ0,sQuery(id+"F0.wireOp",EDGE,"E15")]}),-1.0]])],"derivedFrom":subQ0})])],"isStart":false});}
            var Q24;
            {var subQ0=sQuery(id+"F0.wireOp",EDGE,"E13");Q24=makeQuery(id+"F1.opExtrude","CAP_EDGE",EDGE,{"disambiguationData":[OSD([subQ0]),TDD([makeQuery(id+"F0.imprint","IMPRINT",EDGE,{"disambiguationData":[TD([[makeQuery(id+"F0.imprint","INTERSECT",VERTEX,{"derivedFrom":[subQ0,sQuery(id+"F0.wireOp",EDGE,"E15")]}),-1.0]])],"derivedFrom":subQ0})])],"isStart":false});}
            var Q25;
            {var subQ0=sQuery(id+"F0.wireOp",EDGE,"E8");Q25=makeQuery(id+"F1.opExtrude","CAP_EDGE",EDGE,{"disambiguationData":[OSD([subQ0]),TDD([makeQuery(id+"F0.imprint","IMPRINT",EDGE,{"disambiguationData":[TD([[makeQuery(id+"F0.imprint","INTERSECT",VERTEX,{"derivedFrom":[subQ0,sQuery(id+"F0.wireOp",EDGE,"E17")]}),-1.0]])],"derivedFrom":subQ0})])],"isStart":false});}
            var Q26;
            {var subQ0=sQuery(id+"F0.wireOp",EDGE,"E9");Q26=makeQuery(id+"F1.opExtrude","CAP_EDGE",EDGE,{"disambiguationData":[OSD([subQ0]),TDD([makeQuery(id+"F0.imprint","IMPRINT",EDGE,{"disambiguationData":[TD([[makeQuery(id+"F0.imprint","INTERSECT",VERTEX,{"derivedFrom":[subQ0,sQuery(id+"F0.wireOp",EDGE,"E17")]}),-1.0]])],"derivedFrom":subQ0})])],"isStart":false});}
            var Q27;
            {var subQ0=sQuery(id+"F0.wireOp",EDGE,"E10");Q27=makeQuery(id+"F1.opExtrude","CAP_EDGE",EDGE,{"disambiguationData":[OSD([subQ0]),TDD([makeQuery(id+"F0.imprint","IMPRINT",EDGE,{"disambiguationData":[TD([[makeQuery(id+"F0.imprint","INTERSECT",VERTEX,{"derivedFrom":[subQ0,sQuery(id+"F0.wireOp",EDGE,"E17")]}),-1.0]])],"derivedFrom":subQ0})])],"isStart":false});}
            var Q28;
            {var subQ0=sQuery(id+"F0.wireOp",EDGE,"E11");Q28=makeQuery(id+"F1.opExtrude","CAP_EDGE",EDGE,{"disambiguationData":[OSD([subQ0]),TDD([makeQuery(id+"F0.imprint","IMPRINT",EDGE,{"disambiguationData":[TD([[makeQuery(id+"F0.imprint","INTERSECT",VERTEX,{"derivedFrom":[subQ0,sQuery(id+"F0.wireOp",EDGE,"E17")]}),-1.0]])],"derivedFrom":subQ0})])],"isStart":false});}
            var Q29;
            {var subQ0=sQuery(id+"F0.wireOp",EDGE,"E12");Q29=makeQuery(id+"F1.opExtrude","CAP_EDGE",EDGE,{"disambiguationData":[OSD([subQ0]),TDD([makeQuery(id+"F0.imprint","IMPRINT",EDGE,{"disambiguationData":[TD([[makeQuery(id+"F0.imprint","INTERSECT",VERTEX,{"derivedFrom":[subQ0,sQuery(id+"F0.wireOp",EDGE,"E17")]}),-1.0]])],"derivedFrom":subQ0})])],"isStart":false});}
            var Q30;
            {var subQ0=sQuery(id+"F0.wireOp",EDGE,"E13");Q30=makeQuery(id+"F1.opExtrude","CAP_EDGE",EDGE,{"disambiguationData":[OSD([subQ0]),TDD([makeQuery(id+"F0.imprint","IMPRINT",EDGE,{"disambiguationData":[TD([[makeQuery(id+"F0.imprint","INTERSECT",VERTEX,{"derivedFrom":[subQ0,sQuery(id+"F0.wireOp",EDGE,"E17")]}),-1.0]])],"derivedFrom":subQ0})])],"isStart":false});}
            var Q31;
            Q31=makeQuery(id+"F3.opExtrude","SWEPT_EDGE",EDGE,{"disambiguationData":[OSD([sQuery(id+"F2.wireOp",EDGE,"KLBum8TW-YJ0B-5sS5-SbCJ-48z4D2TFME6R.top"),sQuery(id+"F2.wireOp",EDGE,"KLBum8TW-YJ0B-5sS5-SbCJ-48z4D2TFME6R.left")])]});
            var Q32;
            Q32=makeQuery(id+"F3.opExtrude","SWEPT_EDGE",EDGE,{"disambiguationData":[OSD([sQuery(id+"F2.wireOp",EDGE,"KLBum8TW-YJ0B-5sS5-SbCJ-48z4D2TFME6R.top"),sQuery(id+"F2.wireOp",EDGE,"KLBum8TW-YJ0B-5sS5-SbCJ-48z4D2TFME6R.right")])]});
            var Q33;
            {var subQ0=sQuery(id+"F0.wireOp",EDGE,"E19");Q33=makeQuery(id+"F1.opExtrude","CAP_EDGE",EDGE,{"disambiguationData":[OSD([subQ0]),TDD([makeQuery(id+"F0.imprint","IMPRINT",EDGE,{"disambiguationData":[TD([[makeQuery(id+"F0.imprint","INTERSECT",VERTEX,{"derivedFrom":[sQuery(id+"F0.wireOp",EDGE,"E1.left"),subQ0]}),-1.0]])],"derivedFrom":subQ0})])],"isStart":false});}
            var Q34;
            {var subQ0=sQuery(id+"F0.wireOp",EDGE,"E19");Q34=makeQuery(id+"F1.opExtrude","CAP_EDGE",EDGE,{"disambiguationData":[OSD([subQ0]),TDD([makeQuery(id+"F0.imprint","IMPRINT",EDGE,{"disambiguationData":[TD([[makeQuery(id+"F0.imprint","INTERSECT",VERTEX,{"derivedFrom":[sQuery(id+"F0.wireOp",EDGE,"E9"),subQ0]}),-1.0]])],"derivedFrom":subQ0})])],"isStart":false});}
            var Q35;
            {var subQ0=sQuery(id+"F0.wireOp",EDGE,"E19");Q35=makeQuery(id+"F1.opExtrude","CAP_EDGE",EDGE,{"disambiguationData":[OSD([subQ0]),TDD([makeQuery(id+"F0.imprint","IMPRINT",EDGE,{"disambiguationData":[TD([[makeQuery(id+"F0.imprint","INTERSECT",VERTEX,{"derivedFrom":[sQuery(id+"F0.wireOp",EDGE,"E11"),subQ0]}),-1.0]])],"derivedFrom":subQ0})])],"isStart":false});}
            var Q36;
            {var subQ0=sQuery(id+"F0.wireOp",EDGE,"E19");Q36=makeQuery(id+"F1.opExtrude","CAP_EDGE",EDGE,{"disambiguationData":[OSD([subQ0]),TDD([makeQuery(id+"F0.imprint","IMPRINT",EDGE,{"disambiguationData":[TD([[makeQuery(id+"F0.imprint","INTERSECT",VERTEX,{"derivedFrom":[sQuery(id+"F0.wireOp",EDGE,"E1.right"),subQ0]}),1.0]])],"derivedFrom":subQ0})])],"isStart":false});}
            var Q37;
            {var subQ0=sQuery(id+"F0.wireOp",EDGE,"E13");Q37=makeQuery(id+"F1.opExtrude","CAP_EDGE",EDGE,{"disambiguationData":[OSD([subQ0]),TDD([makeQuery(id+"F0.imprint","IMPRINT",EDGE,{"disambiguationData":[TD([[makeQuery(id+"F0.imprint","INTERSECT",VERTEX,{"derivedFrom":[sQuery(id+"F0.wireOp",EDGE,"E1.top"),subQ0]}),1.0]])],"derivedFrom":subQ0})])],"isStart":false});}
            var Q38;
            {var subQ0=sQuery(id+"F0.wireOp",EDGE,"E12");Q38=makeQuery(id+"F1.opExtrude","CAP_EDGE",EDGE,{"disambiguationData":[OSD([subQ0]),TDD([makeQuery(id+"F0.imprint","IMPRINT",EDGE,{"disambiguationData":[TD([[makeQuery(id+"F0.imprint","INTERSECT",VERTEX,{"derivedFrom":[sQuery(id+"F0.wireOp",EDGE,"E1.top"),subQ0]}),1.0]])],"derivedFrom":subQ0})])],"isStart":false});}
            var Q39;
            {var subQ0=sQuery(id+"F0.wireOp",EDGE,"E18");Q39=makeQuery(id+"F1.opExtrude","CAP_EDGE",EDGE,{"disambiguationData":[OSD([subQ0]),TDD([makeQuery(id+"F0.imprint","IMPRINT",EDGE,{"disambiguationData":[TD([[makeQuery(id+"F0.imprint","INTERSECT",VERTEX,{"derivedFrom":[sQuery(id+"F0.wireOp",EDGE,"E1.right"),subQ0]}),1.0]])],"derivedFrom":subQ0})])],"isStart":false});}
            var Q40;
            {var subQ0=sQuery(id+"F0.wireOp",EDGE,"E18");Q40=makeQuery(id+"F1.opExtrude","CAP_EDGE",EDGE,{"disambiguationData":[OSD([subQ0]),TDD([makeQuery(id+"F0.imprint","IMPRINT",EDGE,{"disambiguationData":[TD([[makeQuery(id+"F0.imprint","INTERSECT",VERTEX,{"derivedFrom":[sQuery(id+"F0.wireOp",EDGE,"E11"),subQ0]}),-1.0]])],"derivedFrom":subQ0})])],"isStart":false});}
            var Q41;
            {var subQ0=sQuery(id+"F0.wireOp",EDGE,"E11");Q41=makeQuery(id+"F1.opExtrude","CAP_EDGE",EDGE,{"disambiguationData":[OSD([subQ0]),TDD([makeQuery(id+"F0.imprint","IMPRINT",EDGE,{"disambiguationData":[TD([[makeQuery(id+"F0.imprint","INTERSECT",VERTEX,{"derivedFrom":[sQuery(id+"F0.wireOp",EDGE,"E1.top"),subQ0]}),1.0]])],"derivedFrom":subQ0})])],"isStart":false});}
            var Q42;
            {var subQ0=sQuery(id+"F0.wireOp",EDGE,"E10");Q42=makeQuery(id+"F1.opExtrude","CAP_EDGE",EDGE,{"disambiguationData":[OSD([subQ0]),TDD([makeQuery(id+"F0.imprint","IMPRINT",EDGE,{"disambiguationData":[TD([[makeQuery(id+"F0.imprint","INTERSECT",VERTEX,{"derivedFrom":[sQuery(id+"F0.wireOp",EDGE,"E1.top"),subQ0]}),1.0]])],"derivedFrom":subQ0})])],"isStart":false});}
            var Q43;
            {var subQ0=sQuery(id+"F0.wireOp",EDGE,"E18");Q43=makeQuery(id+"F1.opExtrude","CAP_EDGE",EDGE,{"disambiguationData":[OSD([subQ0]),TDD([makeQuery(id+"F0.imprint","IMPRINT",EDGE,{"disambiguationData":[TD([[makeQuery(id+"F0.imprint","INTERSECT",VERTEX,{"derivedFrom":[sQuery(id+"F0.wireOp",EDGE,"E9"),subQ0]}),-1.0]])],"derivedFrom":subQ0})])],"isStart":false});}
            var Q44;
            {var subQ0=sQuery(id+"F0.wireOp",EDGE,"E9");Q44=makeQuery(id+"F1.opExtrude","CAP_EDGE",EDGE,{"disambiguationData":[OSD([subQ0]),TDD([makeQuery(id+"F0.imprint","IMPRINT",EDGE,{"disambiguationData":[TD([[makeQuery(id+"F0.imprint","INTERSECT",VERTEX,{"derivedFrom":[sQuery(id+"F0.wireOp",EDGE,"E1.top"),subQ0]}),1.0]])],"derivedFrom":subQ0})])],"isStart":false});}
            var Q45;
            {var subQ0=sQuery(id+"F0.wireOp",EDGE,"E18");Q45=makeQuery(id+"F1.opExtrude","CAP_EDGE",EDGE,{"disambiguationData":[OSD([subQ0]),TDD([makeQuery(id+"F0.imprint","IMPRINT",EDGE,{"disambiguationData":[TD([[makeQuery(id+"F0.imprint","INTERSECT",VERTEX,{"derivedFrom":[sQuery(id+"F0.wireOp",EDGE,"E1.left"),subQ0]}),-1.0]])],"derivedFrom":subQ0})])],"isStart":false});}
            var Q46;
            {var subQ0=sQuery(id+"F0.wireOp",EDGE,"E8");Q46=makeQuery(id+"F1.opExtrude","CAP_EDGE",EDGE,{"disambiguationData":[OSD([subQ0]),TDD([makeQuery(id+"F0.imprint","IMPRINT",EDGE,{"disambiguationData":[TD([[makeQuery(id+"F0.imprint","INTERSECT",VERTEX,{"derivedFrom":[sQuery(id+"F0.wireOp",EDGE,"E1.top"),subQ0]}),1.0]])],"derivedFrom":subQ0})])],"isStart":false});}
            var Q47;
            {var subQ0=sQuery(id+"F0.wireOp",EDGE,"E1.top");Q47=makeQuery(id+"F1.opExtrude","CAP_EDGE",EDGE,{"disambiguationData":[OSD([subQ0]),TDD([makeQuery(id+"F0.imprint","IMPRINT",EDGE,{"disambiguationData":[TD([[makeQuery(id+"F0.imprint","INTERSECT",VERTEX,{"derivedFrom":[subQ0,sQuery(id+"F0.wireOp",EDGE,"E1.left")]}),-1.0]])],"derivedFrom":subQ0})])],"isStart":false});}
            var Q48;
            {var subQ0=sQuery(id+"F0.wireOp",EDGE,"E1.top");Q48=makeQuery(id+"F1.opExtrude","CAP_EDGE",EDGE,{"disambiguationData":[OSD([subQ0]),TDD([makeQuery(id+"F0.imprint","IMPRINT",EDGE,{"disambiguationData":[TD([[makeQuery(id+"F0.imprint","INTERSECT",VERTEX,{"derivedFrom":[subQ0,sQuery(id+"F0.wireOp",EDGE,"E9")]}),-1.0]])],"derivedFrom":subQ0})])],"isStart":false});}
            var Q49;
            {var subQ0=sQuery(id+"F0.wireOp",EDGE,"E1.top");Q49=makeQuery(id+"F1.opExtrude","CAP_EDGE",EDGE,{"disambiguationData":[OSD([subQ0]),TDD([makeQuery(id+"F0.imprint","IMPRINT",EDGE,{"disambiguationData":[TD([[makeQuery(id+"F0.imprint","INTERSECT",VERTEX,{"derivedFrom":[subQ0,sQuery(id+"F0.wireOp",EDGE,"E11")]}),-1.0]])],"derivedFrom":subQ0})])],"isStart":false});}
            var Q50;
            {var subQ0=sQuery(id+"F0.wireOp",EDGE,"E1.top");Q50=makeQuery(id+"F1.opExtrude","CAP_EDGE",EDGE,{"disambiguationData":[OSD([subQ0]),TDD([makeQuery(id+"F0.imprint","IMPRINT",EDGE,{"disambiguationData":[TD([[makeQuery(id+"F0.imprint","INTERSECT",VERTEX,{"derivedFrom":[subQ0,sQuery(id+"F0.wireOp",EDGE,"E1.right")]}),1.0]])],"derivedFrom":subQ0})])],"isStart":false});}
            var Q51;
            Q51=makeQuery(id+"F1.opExtrude","CAP_EDGE",EDGE,{"disambiguationData":[OSD([sQuery(id+"F0.wireOp",EDGE,"E0.right")])],"isStart":true});
            var Q52;
            {var subQ0=sQuery(id+"F0.wireOp",EDGE,"E1.top");Q52=makeQuery(id+"F1.opExtrude","CAP_EDGE",EDGE,{"disambiguationData":[OSD([subQ0]),TDD([makeQuery(id+"F0.imprint","IMPRINT",EDGE,{"disambiguationData":[TD([[makeQuery(id+"F0.imprint","INTERSECT",VERTEX,{"derivedFrom":[subQ0,sQuery(id+"F0.wireOp",EDGE,"E1.right")]}),1.0]])],"derivedFrom":subQ0})])],"isStart":true});}
            var Q53;
            {var subQ0=sQuery(id+"F0.wireOp",EDGE,"E1.top");Q53=makeQuery(id+"F1.opExtrude","CAP_EDGE",EDGE,{"disambiguationData":[OSD([subQ0]),TDD([makeQuery(id+"F0.imprint","IMPRINT",EDGE,{"disambiguationData":[TD([[makeQuery(id+"F0.imprint","INTERSECT",VERTEX,{"derivedFrom":[subQ0,sQuery(id+"F0.wireOp",EDGE,"E11")]}),-1.0]])],"derivedFrom":subQ0})])],"isStart":true});}
            var Q54;
            {var subQ0=sQuery(id+"F0.wireOp",EDGE,"E1.top");Q54=makeQuery(id+"F1.opExtrude","CAP_EDGE",EDGE,{"disambiguationData":[OSD([subQ0]),TDD([makeQuery(id+"F0.imprint","IMPRINT",EDGE,{"disambiguationData":[TD([[makeQuery(id+"F0.imprint","INTERSECT",VERTEX,{"derivedFrom":[subQ0,sQuery(id+"F0.wireOp",EDGE,"E9")]}),-1.0]])],"derivedFrom":subQ0})])],"isStart":true});}
            var Q55;
            {var subQ0=sQuery(id+"F0.wireOp",EDGE,"E1.top");Q55=makeQuery(id+"F1.opExtrude","CAP_EDGE",EDGE,{"disambiguationData":[OSD([subQ0]),TDD([makeQuery(id+"F0.imprint","IMPRINT",EDGE,{"disambiguationData":[TD([[makeQuery(id+"F0.imprint","INTERSECT",VERTEX,{"derivedFrom":[subQ0,sQuery(id+"F0.wireOp",EDGE,"E1.left")]}),-1.0]])],"derivedFrom":subQ0})])],"isStart":true});}
            var Q56;
            {var subQ0=sQuery(id+"F0.wireOp",EDGE,"E1.bottom");Q56=makeQuery(id+"F1.opExtrude","CAP_EDGE",EDGE,{"disambiguationData":[OSD([subQ0]),TDD([makeQuery(id+"F0.imprint","IMPRINT",EDGE,{"disambiguationData":[TD([[makeQuery(id+"F0.imprint","INTERSECT",VERTEX,{"derivedFrom":[subQ0,sQuery(id+"F0.wireOp",EDGE,"E1.right")]}),1.0]])],"derivedFrom":subQ0})])],"isStart":true});}
            var Q57;
            {var subQ0=sQuery(id+"F0.wireOp",EDGE,"E1.bottom");Q57=makeQuery(id+"F1.opExtrude","CAP_EDGE",EDGE,{"disambiguationData":[OSD([subQ0]),TDD([makeQuery(id+"F0.imprint","IMPRINT",EDGE,{"disambiguationData":[TD([[makeQuery(id+"F0.imprint","INTERSECT",VERTEX,{"derivedFrom":[subQ0,sQuery(id+"F0.wireOp",EDGE,"E11")]}),-1.0]])],"derivedFrom":subQ0})])],"isStart":true});}
            var Q58;
            {var subQ0=sQuery(id+"F0.wireOp",EDGE,"E1.bottom");Q58=makeQuery(id+"F1.opExtrude","CAP_EDGE",EDGE,{"disambiguationData":[OSD([subQ0]),TDD([makeQuery(id+"F0.imprint","IMPRINT",EDGE,{"disambiguationData":[TD([[makeQuery(id+"F0.imprint","INTERSECT",VERTEX,{"derivedFrom":[subQ0,sQuery(id+"F0.wireOp",EDGE,"E9")]}),-1.0]])],"derivedFrom":subQ0})])],"isStart":true});}
            var Q59;
            {var subQ0=sQuery(id+"F0.wireOp",EDGE,"E1.bottom");Q59=makeQuery(id+"F1.opExtrude","CAP_EDGE",EDGE,{"disambiguationData":[OSD([subQ0]),TDD([makeQuery(id+"F0.imprint","IMPRINT",EDGE,{"disambiguationData":[TD([[makeQuery(id+"F0.imprint","INTERSECT",VERTEX,{"derivedFrom":[subQ0,sQuery(id+"F0.wireOp",EDGE,"E1.left")]}),-1.0]])],"derivedFrom":subQ0})])],"isStart":true});}
            var Q60;
            Q60=makeQuery(id+"F1.opExtrude","CAP_EDGE",EDGE,{"disambiguationData":[OSD([sQuery(id+"F0.wireOp",EDGE,"E0.bottom")])],"isStart":false});
            var Q61;
            Q61=makeQuery(id+"F3.opExtrude","CAP_EDGE",EDGE,{"disambiguationData":[OSD([sQuery(id+"F2.wireOp",EDGE,"KLBum8TW-YJ0B-5sS5-SbCJ-48z4D2TFME6R.top")])],"isStart":true});
            var Q62;
            Q62=makeQuery(id+"F3.opExtrude","CAP_EDGE",EDGE,{"disambiguationData":[OSD([sQuery(id+"F2.wireOp",EDGE,"KLBum8TW-YJ0B-5sS5-SbCJ-48z4D2TFME6R.top")])],"isStart":false});
            var Q63;
            {var subQ0=sQuery(id+"F0.wireOp",EDGE,"E16");Q63=makeQuery(id+"F1.opExtrude","CAP_EDGE",EDGE,{"disambiguationData":[OSD([subQ0]),TDD([makeQuery(id+"F0.imprint","IMPRINT",EDGE,{"disambiguationData":[TD([[makeQuery(id+"F0.imprint","INTERSECT",VERTEX,{"derivedFrom":[sQuery(id+"F0.wireOp",EDGE,"E11"),subQ0]}),-1.0]])],"derivedFrom":subQ0})])],"isStart":false});}
            var Q64;
            {var subQ0=sQuery(id+"F0.wireOp",EDGE,"E16");Q64=makeQuery(id+"F1.opExtrude","CAP_EDGE",EDGE,{"disambiguationData":[OSD([subQ0]),TDD([makeQuery(id+"F0.imprint","IMPRINT",EDGE,{"disambiguationData":[TD([[makeQuery(id+"F0.imprint","INTERSECT",VERTEX,{"derivedFrom":[sQuery(id+"F0.wireOp",EDGE,"E9"),subQ0]}),-1.0]])],"derivedFrom":subQ0})])],"isStart":false});}
            var Q65;
            {var subQ0=sQuery(id+"F0.wireOp",EDGE,"E16");Q65=makeQuery(id+"F1.opExtrude","CAP_EDGE",EDGE,{"disambiguationData":[OSD([subQ0]),TDD([makeQuery(id+"F0.imprint","IMPRINT",EDGE,{"disambiguationData":[TD([[makeQuery(id+"F0.imprint","INTERSECT",VERTEX,{"derivedFrom":[sQuery(id+"F0.wireOp",EDGE,"E1.left"),subQ0]}),-1.0]])],"derivedFrom":subQ0})])],"isStart":false});}
            var Q66;
            {var subQ0=sQuery(id+"F0.wireOp",EDGE,"E17");Q66=makeQuery(id+"F1.opExtrude","CAP_EDGE",EDGE,{"disambiguationData":[OSD([subQ0]),TDD([makeQuery(id+"F0.imprint","IMPRINT",EDGE,{"disambiguationData":[TD([[makeQuery(id+"F0.imprint","INTERSECT",VERTEX,{"derivedFrom":[sQuery(id+"F0.wireOp",EDGE,"E11"),subQ0]}),-1.0]])],"derivedFrom":subQ0})])],"isStart":false});}
            var Q67;
            {var subQ0=sQuery(id+"F0.wireOp",EDGE,"E17");Q67=makeQuery(id+"F1.opExtrude","CAP_EDGE",EDGE,{"disambiguationData":[OSD([subQ0]),TDD([makeQuery(id+"F0.imprint","IMPRINT",EDGE,{"disambiguationData":[TD([[makeQuery(id+"F0.imprint","INTERSECT",VERTEX,{"derivedFrom":[sQuery(id+"F0.wireOp",EDGE,"E9"),subQ0]}),-1.0]])],"derivedFrom":subQ0})])],"isStart":false});}
            var Q68;
            {var subQ0=sQuery(id+"F0.wireOp",EDGE,"E17");Q68=makeQuery(id+"F1.opExtrude","CAP_EDGE",EDGE,{"disambiguationData":[OSD([subQ0]),TDD([makeQuery(id+"F0.imprint","IMPRINT",EDGE,{"disambiguationData":[TD([[makeQuery(id+"F0.imprint","INTERSECT",VERTEX,{"derivedFrom":[sQuery(id+"F0.wireOp",EDGE,"E1.left"),subQ0]}),-1.0]])],"derivedFrom":subQ0})])],"isStart":false});}
            var Q69;
            {var subQ0=sQuery(id+"F0.wireOp",EDGE,"E1.right");Q69=makeQuery(id+"F1.opExtrude","CAP_EDGE",EDGE,{"disambiguationData":[OSD([subQ0]),TDD([makeQuery(id+"F0.imprint","IMPRINT",EDGE,{"disambiguationData":[TD([[makeQuery(id+"F0.imprint","INTERSECT",VERTEX,{"derivedFrom":[sQuery(id+"F0.wireOp",EDGE,"E1.bottom"),subQ0]}),-1.0]])],"derivedFrom":subQ0})])],"isStart":false});}
            var Q70;
            {var subQ0=sQuery(id+"F0.wireOp",EDGE,"E1.right");Q70=makeQuery(id+"F1.opExtrude","CAP_EDGE",EDGE,{"disambiguationData":[OSD([subQ0]),TDD([makeQuery(id+"F0.imprint","IMPRINT",EDGE,{"disambiguationData":[TD([[makeQuery(id+"F0.imprint","INTERSECT",VERTEX,{"derivedFrom":[subQ0,sQuery(id+"F0.wireOp",EDGE,"E15")]}),-1.0]])],"derivedFrom":subQ0})])],"isStart":false});}
            var Q71;
            {var subQ0=sQuery(id+"F0.wireOp",EDGE,"E1.right");Q71=makeQuery(id+"F1.opExtrude","CAP_EDGE",EDGE,{"disambiguationData":[OSD([subQ0]),TDD([makeQuery(id+"F0.imprint","IMPRINT",EDGE,{"disambiguationData":[TD([[makeQuery(id+"F0.imprint","INTERSECT",VERTEX,{"derivedFrom":[subQ0,sQuery(id+"F0.wireOp",EDGE,"E17")]}),-1.0]])],"derivedFrom":subQ0})])],"isStart":false});}
            var Q72;
            {var subQ0=sQuery(id+"F0.wireOp",EDGE,"E1.right");Q72=makeQuery(id+"F1.opExtrude","CAP_EDGE",EDGE,{"disambiguationData":[OSD([subQ0]),TDD([makeQuery(id+"F0.imprint","IMPRINT",EDGE,{"disambiguationData":[TD([[makeQuery(id+"F0.imprint","INTERSECT",VERTEX,{"derivedFrom":[sQuery(id+"F0.wireOp",EDGE,"E1.top"),subQ0]}),1.0]])],"derivedFrom":subQ0})])],"isStart":false});}
            fillet(context, id + "F7", {"entities" : qUnion([Q0, Q1, Q2, Q3, Q4, Q5, Q6, Q7, Q8, Q9, Q10, Q11, Q12, Q13, Q14, Q15, Q16, Q17, Q18, Q19, Q20, Q21, Q22, Q23, Q24, Q25, Q26, Q27, Q28, Q29, Q30, Q31, Q32, Q33, Q34, Q35, Q36, Q37, Q38, Q39, Q40, Q41, Q42, Q43, Q44, Q45, Q46, Q47, Q48, Q49, Q50, Q51, Q52, Q53, Q54, Q55, Q56, Q57, Q58, Q59, Q60, Q61, Q62, Q63, Q64, Q65, Q66, Q67, Q68, Q69, Q70, Q71, Q72]), "radius" : 1 * mm, "tangentPropagation" : true, "allowEdgeOverflow" : false});
        }
        {
            var Q0;
            Q0=qCreatedBy(makeId("Front.planeOp"),FACE);
            var sketch = newSketch(context, id + "F8", { "sketchPlane" : qUnion([Q0])});
            skLineSegment(sketch, "E23.bottom", {"start": v(24, 41) * mm, "end": v(29, 41) * mm});
            skLineSegment(sketch, "E23.top", {"start": v(24, 35) * mm, "end": v(29, 35) * mm});
            skLineSegment(sketch, "E23.left", {"start": v(24, 41) * mm, "end": v(24, 35) * mm});
            skLineSegment(sketch, "E23.right", {"start": v(29, 41) * mm, "end": v(29, 35) * mm});
            skSolve(sketch);
        }
        {
            var Q0;
            Q0 = qSketchRegion(id + "F8", true);
            extrude(context, id + "F9", {"entities" : qUnion([Q0]), "operationType" : NewBodyOperationType.ADD, "depth" : 10 * mm, "offsetDistance" : 25 * mm});
        }
        {
            var Q0;
            Q0=qCreatedBy(makeId("Right.planeOp"),FACE);
            var sketch = newSketch(context, id + "F10", { "sketchPlane" : qUnion([Q0])});
            skPoint(sketch, "E24", {"position": v(-6, 38) * mm});
            skSolve(sketch);
        }
        {
            var Q0;
            Q0=sQuery(id+"F10.wireOp",VERTEX,"E24");
            var Q1;
            Q1=makeQuery(id+"F1.opExtrude","SWEPT_BODY",BODY,{"disambiguationData":[OSD([sQuery(id+"F0.wireOp",EDGE,"E0.bottom"),sQuery(id+"F0.wireOp",EDGE,"E0.top"),sQuery(id+"F0.wireOp",EDGE,"E0.left"),sQuery(id+"F0.wireOp",EDGE,"E0.right"),sQuery(id+"F0.wireOp",EDGE,"E1.bottom"),sQuery(id+"F0.wireOp",EDGE,"E1.top"),sQuery(id+"F0.wireOp",EDGE,"E1.left"),sQuery(id+"F0.wireOp",EDGE,"E1.right"),sQuery(id+"F0.wireOp",EDGE,"E8"),sQuery(id+"F0.wireOp",EDGE,"E9"),sQuery(id+"F0.wireOp",EDGE,"E10"),sQuery(id+"F0.wireOp",EDGE,"E11"),sQuery(id+"F0.wireOp",EDGE,"E12"),sQuery(id+"F0.wireOp",EDGE,"E13"),sQuery(id+"F0.wireOp",EDGE,"E14"),sQuery(id+"F0.wireOp",EDGE,"E15"),sQuery(id+"F0.wireOp",EDGE,"E16"),sQuery(id+"F0.wireOp",EDGE,"E17"),sQuery(id+"F0.wireOp",EDGE,"E18"),sQuery(id+"F0.wireOp",EDGE,"E19")])]});
            hole(context, id + "F11", {"style" : HoleStyle.SIMPLE, "endStyle" : HoleEndStyle.BLIND, "oppositeDirection" : true, "holeDiameter" : 2 * mm, "majorDiameter" : 5 * mm, "holeDepth" : 40 * mm, "isTappedThrough" : true, "tappedDepth" : 12 * mm, "tapClearance" : 3, "locations" : qUnion([Q0]), "scope" : qUnion([Q1])});
        }
        {
            var Q0;
            Q0=makeQuery(id+"F9.opExtrude","CAP_EDGE",EDGE,{"disambiguationData":[OSD([sQuery(id+"F8.wireOp",EDGE,"E23.bottom")])],"isStart":false});
            var Q1;
            Q1=makeQuery(id+"F9.opExtrude","CAP_EDGE",EDGE,{"disambiguationData":[OSD([sQuery(id+"F8.wireOp",EDGE,"E23.top")])],"isStart":false});
            var Q2;
            Q2=makeQuery(id+"F9.opExtrude","CAP_EDGE",EDGE,{"disambiguationData":[OSD([sQuery(id+"F8.wireOp",EDGE,"E23.left")])],"isStart":false});
            fillet(context, id + "F12", {"entities" : qUnion([Q0, Q1, Q2]), "radius" : 2 * mm, "tangentPropagation" : true, "allowEdgeOverflow" : false});
        }
    });
